# Revit family: Haworth_HATElements_BenchDouble_AP_PRELIMINARY
name_source: partatom
category: Furniture
units: mm (PartAtom-declared; Revit-internal decimal feet)

## family parameters
Always vertical = Yes
Cut with Voids When Loaded = No
OmniClass Number = 23.40.70.14.64.11
OmniClass Title = Office Furniture
Room Calculation Point = No
Shared = No
Work Plane-Based = No

## types (6) — shared parameters
Assembly Code = E2020200
Base Tube Finish = Haworth _ Paint _ Smoke
Box Body Finish = Haworth _ Paint _ Black
Cable Tray Finish = Haworth _ Polymer _ Undecided
Cable Tray Width = 600 mm
Description = Haworth - HAT Elements - Double Bench
Flip Top Finish = Haworth _ Paint _ Metallic Silver
Manufacturer = Haworth
Model = SYELDBXXXX
Revision Number = 1
Size = Verify Final Dim.w/ Haworth
Trim Finish = Haworth _ Metal _ Structured White EC
URL = https://www.haworth.com
URL - Product = https://www.haworth.com
Warranty = http://www.haworth.com
Worksurface Depth = 1200, 1400, 1500, 1600 mm
Worksurface Width = 1200, 1400, 1500, 1600, 1800 mm
with Worktop = Yes
without Height Adjustment = Yes

## per-type parameters (varying)
| type | Actual Depth | Actual Height | Actual Width | Double Cable Trunk Heavy Duty | Double Cable Trunk Normal | Flip Top Cable Outlet | Handcrank | Leg Height | Rectangular Motorized | Round Leg | Round Motorized | Square Leg | Square Motorized | Umbilical Cord to Floor | Umbilical Cord to Trunk | Understructure Width | with Height Adjustment | without Cable Trunk |
| 1800 x 1600 | 800 mm  [stored 2.62467 ft] | 800 mm  [stored 2.62467 ft] | 1800 mm  [stored 5.90551 ft] | No | Yes | Yes | No | 765 mm  [stored 2.50984 ft] | No | No | No | Yes | Yes | No | Yes | 1680 mm  [stored 5.51181 ft] | Yes | No |
| 1200 x 1200 | 600 mm | 730 mm  [stored 2.39501 ft] | 1200 mm | Yes | No | Yes | No | 695 mm  [stored 2.28018 ft] | No | Yes | Yes | No | No | Yes | No | 1080 mm  [stored 3.54331 ft] | Yes | No |
| 1500 x 1400 | 700 mm  [stored 2.29659 ft] | 730 mm  [stored 2.39501 ft] | 1500 mm  [stored 4.92126 ft] | No | No | No | No | 695 mm  [stored 2.28018 ft] | Yes | No | No | Yes | No | No | No | 1380 mm  [stored 4.52756 ft] | Yes | Yes |
| 1000 x 1500 | 750 mm  [stored 2.46063 ft] | 730 mm  [stored 2.39501 ft] | 1000 mm  [stored 3.28084 ft] | No | No | No | No | 695 mm  [stored 2.28018 ft] | No | No | No | Yes | No | No | No | 880 mm  [stored 2.88714 ft] | No | Yes |
| 1600 x 1500 | 750 mm  [stored 2.46063 ft] | 730 mm  [stored 2.39501 ft] | 1600 mm  [stored 5.24934 ft] | Yes | No | Yes | No | 695 mm  [stored 2.28018 ft] | Yes | No | No | Yes | No | Yes | No | 1480 mm  [stored 4.85564 ft] | Yes | No |
| 1400 x 1600 | 800 mm  [stored 2.62467 ft] | 730 mm  [stored 2.39501 ft] | 1400 mm  [stored 4.59318 ft] | No | Yes | Yes | Yes | 695 mm  [stored 2.28018 ft] | No | No | No | Yes | No | No | Yes | 1280 mm  [stored 4.19948 ft] | Yes | No |

note: [stored X ft] marks values corroborated as IEEE doubles in the binary element streams (Revit-internal decimal feet)

## geometry (parser evidence)
native form markers: Sweep x37
no freeform markers — native parametric forms only
